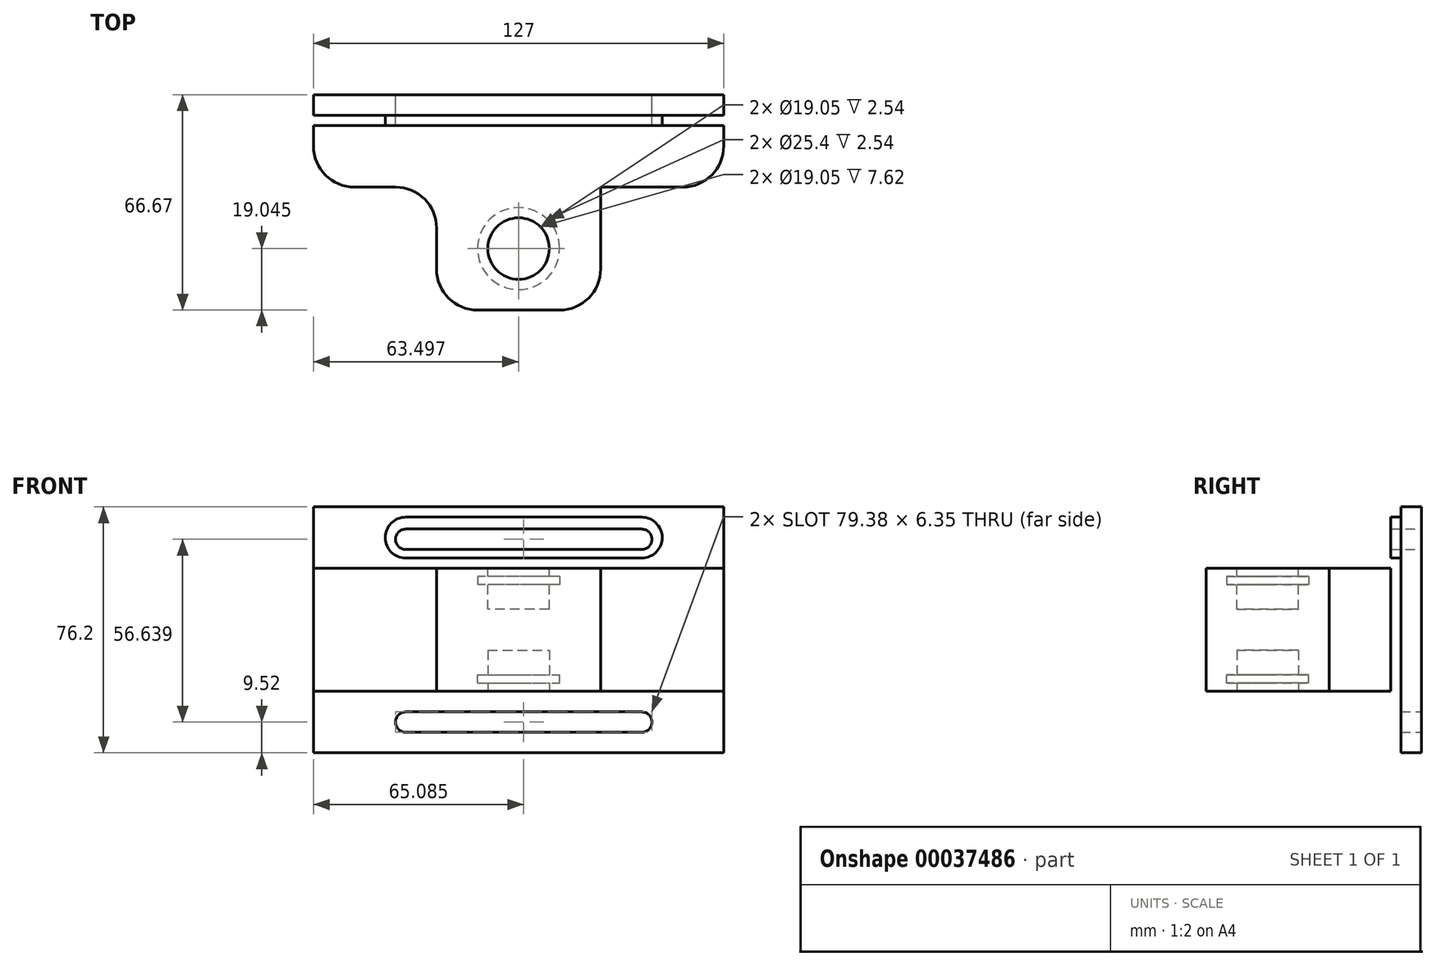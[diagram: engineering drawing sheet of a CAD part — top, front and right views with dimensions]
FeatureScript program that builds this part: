
annotation { "Feature Type Name" : "Feature", "Feature Type Description" : "" }
export const myFeature = defineFeature(function(context is Context, id is Id, definition is map)
    precondition{}
    {
        {
            var Q0;
            Q0=qCreatedBy(makeId("Front.planeOp"),FACE);
            var sketch = newSketch(context, id + "F0", { "sketchPlane" : qUnion([Q0])});
            skLineSegment(sketch, "E0.bottom", {"start": v(-62.5, -34.76) * mm, "end": v(64.5, -34.76) * mm});
            skLineSegment(sketch, "E0.top", {"start": v(-62.5, 41.44) * mm, "end": v(64.5, 41.44) * mm});
            skLineSegment(sketch, "E0.left", {"start": v(-62.5, -34.76) * mm, "end": v(-62.5, 41.44) * mm});
            skLineSegment(sketch, "E0.right", {"start": v(64.5, -34.76) * mm, "end": v(64.5, 41.44) * mm});
            skArc(sketch, "E1", {"start": v(-33.93, -22.06) * mm, "mid": v(-37.1, -25.24) * mm, "end": v(-33.93, -28.41) * mm});
            skArc(sketch, "E2", {"start": v(39.1, -28.41) * mm, "mid": v(42.27, -25.24) * mm, "end": v(39.1, -22.06) * mm});
            skLineSegment(sketch, "E3", {"start": v(-33.93, -22.06) * mm, "end": v(39.1, -22.06) * mm});
            skLineSegment(sketch, "E4", {"start": v(-33.93, -28.41) * mm, "end": v(39.1, -28.41) * mm});
            skLineSegment(sketch, "E5", {"start": v(-62.5, 3.08) * mm, "end": v(64.5, 3.08) * mm, "construction": true});
            skArc(sketch, "E6.MirrorCS", {"start": v(-33.93, 28.22) * mm, "mid": v(-37.1, 31.4) * mm, "end": v(-33.93, 34.57) * mm});
            skLineSegment(sketch, "E7.MirrorCS", {"start": v(-33.93, 28.22) * mm, "end": v(39.1, 28.22) * mm});
            skLineSegment(sketch, "E8.MirrorCS", {"start": v(-33.93, 34.57) * mm, "end": v(39.1, 34.57) * mm});
            skArc(sketch, "E9.MirrorCS", {"start": v(39.1, 34.57) * mm, "mid": v(42.27, 31.4) * mm, "end": v(39.1, 28.22) * mm});
            skSolve(sketch);
        }
        {
            var Q0;
            Q0=makeQuery(id+"F0.imprint","IMPRINT",FACE,{"disambiguationData":[TD([[makeQuery(id+"F0.imprint","IMPRINT",EDGE,{"derivedFrom":sQuery(id+"F0.wireOp",EDGE,"E0.bottom")}),1.0]])]});
            extrude(context, id + "F1", {"entities" : qUnion([Q0]), "depth" : 9.52 * mm});
        }
        {
            var Q0;
            Q0=makeQuery(id+"F1.opExtrude","CAP_FACE",FACE,{"disambiguationData":[OSD([sQuery(id+"F0.wireOp",EDGE,"E0.bottom"),sQuery(id+"F0.wireOp",EDGE,"E0.top"),sQuery(id+"F0.wireOp",EDGE,"E0.left"),sQuery(id+"F0.wireOp",EDGE,"E0.right"),sQuery(id+"F0.wireOp",EDGE,"E1"),sQuery(id+"F0.wireOp",EDGE,"E2"),sQuery(id+"F0.wireOp",EDGE,"E3"),sQuery(id+"F0.wireOp",EDGE,"E4"),sQuery(id+"F0.wireOp",EDGE,"E6.MirrorCS"),sQuery(id+"F0.wireOp",EDGE,"E7.MirrorCS"),sQuery(id+"F0.wireOp",EDGE,"E8.MirrorCS"),sQuery(id+"F0.wireOp",EDGE,"E9.MirrorCS")])],"isStart":false});
            var sketch = newSketch(context, id + "F2", { "sketchPlane" : qUnion([Q0])});
            skArc(sketch, "E10", {"start": v(-33.93, -18.89) * mm, "mid": v(-40.28, -25.24) * mm, "end": v(-33.93, -31.59) * mm});
            skArc(sketch, "E11", {"start": v(39.1, -31.59) * mm, "mid": v(45.45, -25.24) * mm, "end": v(39.1, -18.89) * mm});
            skLineSegment(sketch, "E12", {"start": v(-33.93, -18.89) * mm, "end": v(39.1, -18.89) * mm});
            skLineSegment(sketch, "E13", {"start": v(-33.93, -31.59) * mm, "end": v(39.1, -31.59) * mm});
            skLineSegment(sketch, "E14", {"start": v(-62.5, 3.34) * mm, "end": v(64.5, 3.34) * mm, "construction": true});
            skArc(sketch, "E15.MirrorCS", {"start": v(-33.93, 25.56) * mm, "mid": v(-40.28, 31.91) * mm, "end": v(-33.93, 38.26) * mm});
            skLineSegment(sketch, "E16.MirrorCS", {"start": v(-33.93, 25.56) * mm, "end": v(39.1, 25.56) * mm});
            skLineSegment(sketch, "E17.MirrorCS", {"start": v(-33.93, 38.26) * mm, "end": v(39.1, 38.26) * mm});
            skArc(sketch, "E18.MirrorCS", {"start": v(39.1, 38.26) * mm, "mid": v(45.45, 31.91) * mm, "end": v(39.1, 25.56) * mm});
            skSolve(sketch);
        }
        {
            var Q0;
            Q0=makeQuery(id+"F2.imprint","IMPRINT",FACE,{"disambiguationData":[TD([[makeQuery(id+"F2.imprint","IMPRINT",EDGE,{"derivedFrom":sQuery(id+"F2.wireOp",EDGE,"E10")}),1.0]])]});
            var Q1;
            Q1=makeQuery(id+"F2.imprint","IMPRINT",FACE,{"disambiguationData":[TD([[makeQuery(id+"F2.imprint","IMPRINT",EDGE,{"derivedFrom":sQuery(id+"F2.wireOp",EDGE,"E15.MirrorCS")}),-1.0]])]});
            extrude(context, id + "F3", {"entities" : qUnion([Q0, Q1]), "operationType" : NewBodyOperationType.REMOVE, "oppositeDirection" : true, "depth" : 3.17 * mm});
        }
        {
            var Q0;
            Q0=makeQuery(id+"F1.opExtrude","CAP_FACE",FACE,{"disambiguationData":[OSD([sQuery(id+"F0.wireOp",EDGE,"E0.bottom"),sQuery(id+"F0.wireOp",EDGE,"E0.top"),sQuery(id+"F0.wireOp",EDGE,"E0.left"),sQuery(id+"F0.wireOp",EDGE,"E0.right"),sQuery(id+"F0.wireOp",EDGE,"E1"),sQuery(id+"F0.wireOp",EDGE,"E2"),sQuery(id+"F0.wireOp",EDGE,"E3"),sQuery(id+"F0.wireOp",EDGE,"E4"),sQuery(id+"F0.wireOp",EDGE,"E6.MirrorCS"),sQuery(id+"F0.wireOp",EDGE,"E7.MirrorCS"),sQuery(id+"F0.wireOp",EDGE,"E8.MirrorCS"),sQuery(id+"F0.wireOp",EDGE,"E9.MirrorCS")])],"isStart":false});
            var sketch = newSketch(context, id + "F4", { "sketchPlane" : qUnion([Q0])});
            skLineSegment(sketch, "E19.bottom", {"start": v(-62.5, -15.71) * mm, "end": v(64.5, -15.71) * mm});
            skLineSegment(sketch, "E19.top", {"start": v(-62.5, 22.39) * mm, "end": v(64.5, 22.39) * mm});
            skLineSegment(sketch, "E19.left", {"start": v(-62.5, -15.71) * mm, "end": v(-62.5, 22.39) * mm});
            skLineSegment(sketch, "E19.right", {"start": v(64.5, -15.71) * mm, "end": v(64.5, 22.39) * mm});
            skSolve(sketch);
        }
        {
            var Q0;
            Q0=makeQuery(id+"F4.imprint","IMPRINT",FACE,{"disambiguationData":[TD([[makeQuery(id+"F4.imprint","IMPRINT",EDGE,{"derivedFrom":sQuery(id+"F4.wireOp",EDGE,"E19.bottom")}),1.0]])]});
            extrude(context, id + "F5", {"entities" : qUnion([Q0]), "operationType" : NewBodyOperationType.ADD, "depth" : 19.05 * mm});
        }
        {
            var Q0;
            Q0=makeQuery(id+"F5.opExtrude","CAP_FACE",FACE,{"disambiguationData":[OSD([sQuery(id+"F4.wireOp",EDGE,"E19.bottom"),sQuery(id+"F4.wireOp",EDGE,"E19.top"),sQuery(id+"F4.wireOp",EDGE,"E19.left"),sQuery(id+"F4.wireOp",EDGE,"E19.right")])],"isStart":false});
            var sketch = newSketch(context, id + "F6", { "sketchPlane" : qUnion([Q0])});
            skLineSegment(sketch, "E20.bottom", {"start": v(-24.4, -15.71) * mm, "end": v(26.4, -15.71) * mm});
            skLineSegment(sketch, "E20.top", {"start": v(-24.4, 22.39) * mm, "end": v(26.4, 22.39) * mm});
            skLineSegment(sketch, "E20.left", {"start": v(-24.4, -15.71) * mm, "end": v(-24.4, 22.39) * mm});
            skLineSegment(sketch, "E20.right", {"start": v(26.4, -15.71) * mm, "end": v(26.4, 22.39) * mm});
            skSolve(sketch);
        }
        {
            var Q0;
            Q0=makeQuery(id+"F6.imprint","IMPRINT",FACE,{"disambiguationData":[TD([[makeQuery(id+"F6.imprint","IMPRINT",EDGE,{"derivedFrom":sQuery(id+"F6.wireOp",EDGE,"E20.bottom")}),1.0]])]});
            extrude(context, id + "F7", {"entities" : qUnion([Q0]), "operationType" : NewBodyOperationType.ADD, "depth" : 38.1 * mm});
        }
        {
            var Q0;
            Q0=makeQuery(id+"F7.boolean.opBoolean","MERGE",FACE,{"derivedFrom":[makeQuery(id+"F5.opExtrude","SWEPT_FACE",FACE,{"disambiguationData":[OSD([sQuery(id+"F4.wireOp",EDGE,"E19.bottom")])]}),makeQuery(id+"F7.opExtrude","SWEPT_FACE",FACE,{"disambiguationData":[OSD([sQuery(id+"F6.wireOp",EDGE,"E20.bottom")])]})]});
            var sketch = newSketch(context, id + "F8", { "sketchPlane" : qUnion([Q0])});
            skPoint(sketch, "E21", {"position": v(1, 47.63) * mm});
            skSolve(sketch);
        }
        {
            var Q0;
            Q0=sQuery(id+"F8.wireOp",VERTEX,"E21");
            var Q1;
            Q1=makeQuery(id+"F1.opExtrude","SWEPT_BODY",BODY,{"disambiguationData":[OSD([sQuery(id+"F0.wireOp",EDGE,"E0.bottom"),sQuery(id+"F0.wireOp",EDGE,"E0.top"),sQuery(id+"F0.wireOp",EDGE,"E0.left"),sQuery(id+"F0.wireOp",EDGE,"E0.right"),sQuery(id+"F0.wireOp",EDGE,"E1"),sQuery(id+"F0.wireOp",EDGE,"E2"),sQuery(id+"F0.wireOp",EDGE,"E3"),sQuery(id+"F0.wireOp",EDGE,"E4"),sQuery(id+"F0.wireOp",EDGE,"E6.MirrorCS"),sQuery(id+"F0.wireOp",EDGE,"E7.MirrorCS"),sQuery(id+"F0.wireOp",EDGE,"E8.MirrorCS"),sQuery(id+"F0.wireOp",EDGE,"E9.MirrorCS")])]});
            hole(context, id + "F9", {"style" : HoleStyle.SIMPLE, "holeDiameter" : 9.52 * mm, "endStyle" : HoleEndStyle.THROUGH, "locations" : qUnion([Q0]), "scope" : qUnion([Q1])});
        }
        {
            var Q0;
            Q0=makeQuery(id+"F7.boolean.opBoolean","MERGE",FACE,{"derivedFrom":[makeQuery(id+"F5.opExtrude","SWEPT_FACE",FACE,{"disambiguationData":[OSD([sQuery(id+"F4.wireOp",EDGE,"E19.bottom")])]}),makeQuery(id+"F7.opExtrude","SWEPT_FACE",FACE,{"disambiguationData":[OSD([sQuery(id+"F6.wireOp",EDGE,"E20.bottom")])]})]});
            var sketch = newSketch(context, id + "F10", { "sketchPlane" : qUnion([Q0])});
            skCircle(sketch, "E22", {"center": v(1, 47.63) * mm, "radius": 9.53 * mm});
            skSolve(sketch);
        }
        {
            var Q0;
            Q0=makeQuery(id+"F10.imprint","IMPRINT",FACE,{"disambiguationData":[TD([[makeQuery(id+"F10.imprint","IMPRINT",EDGE,{"derivedFrom":sQuery(id+"F10.wireOp",EDGE,"E22")}),1.0]])]});
            extrude(context, id + "F11", {"entities" : qUnion([Q0]), "operationType" : NewBodyOperationType.REMOVE, "oppositeDirection" : true, "depth" : 12.7 * mm});
        }
        {
            var Q0;
            Q0=makeQuery(id+"F7.boolean.opBoolean","MERGE",FACE,{"derivedFrom":[makeQuery(id+"F5.opExtrude","SWEPT_FACE",FACE,{"disambiguationData":[OSD([sQuery(id+"F4.wireOp",EDGE,"E19.top")])]}),makeQuery(id+"F7.opExtrude","SWEPT_FACE",FACE,{"disambiguationData":[OSD([sQuery(id+"F6.wireOp",EDGE,"E20.top")])]})]});
            var sketch = newSketch(context, id + "F12", { "sketchPlane" : qUnion([Q0])});
            skCircle(sketch, "E23", {"center": v(1, -47.63) * mm, "radius": 9.53 * mm});
            skSolve(sketch);
        }
        {
            var Q0;
            Q0 = qSketchRegion(id + "F12", true);
            var Q1;
            Q1=makeQuery(id+"F12.imprint","IMPRINT",FACE,{"disambiguationData":[TD([[makeQuery(id+"F12.imprint","IMPRINT",EDGE,{"derivedFrom":sQuery(id+"F12.wireOp",EDGE,"E23")}),1.0]])]});
            extrude(context, id + "F13", {"entities" : qUnion([Q0, Q1]), "operationType" : NewBodyOperationType.REMOVE, "oppositeDirection" : true, "depth" : 12.7 * mm});
        }
        {
            var Q0;
            Q0=makeQuery(id+"F1.opExtrude","SWEPT_FACE",FACE,{"disambiguationData":[OSD([sQuery(id+"F0.wireOp",EDGE,"E0.top")])]});
            cPlane(context, id + "F14", {"entities" : qUnion([Q0]), "cplaneType" : CPlaneType.OFFSET, "offset" : 24.13 * mm, "oppositeDirection" : true, "width" : 152.4 * mm, "height" : 152.4 * mm});
        }
        {
            var Q0;
            Q0=qCreatedBy(id+"F14.planeOp",FACE);
            var sketch = newSketch(context, id + "F15", { "sketchPlane" : qUnion([Q0])});
            skCircle(sketch, "E24", {"center": v(1, -47.63) * mm, "radius": 12.7 * mm});
            skSolve(sketch);
        }
        {
            var Q0;
            Q0=makeQuery(id+"F1.opExtrude","SWEPT_FACE",FACE,{"disambiguationData":[OSD([sQuery(id+"F0.wireOp",EDGE,"E0.bottom")])]});
            cPlane(context, id + "F16", {"entities" : qUnion([Q0]), "cplaneType" : CPlaneType.OFFSET, "offset" : 24.13 * mm, "oppositeDirection" : true, "width" : 152.4 * mm, "height" : 152.4 * mm});
        }
        {
            var Q0;
            Q0=qCreatedBy(id+"F16.planeOp",FACE);
            var sketch = newSketch(context, id + "F17", { "sketchPlane" : qUnion([Q0])});
            skCircle(sketch, "E25.0", {"center": v(1, 47.63) * mm, "radius": 12.7 * mm});
            skSolve(sketch);
        }
        {
            var Q0;
            Q0 = qSketchRegion(id + "F17", true);
            var Q1;
            Q1=makeQuery(id+"F7.boolean.opBoolean","MERGE",FACE,{"derivedFrom":[makeQuery(id+"F5.opExtrude","SWEPT_FACE",FACE,{"disambiguationData":[OSD([sQuery(id+"F4.wireOp",EDGE,"E19.bottom")])]}),makeQuery(id+"F7.opExtrude","SWEPT_FACE",FACE,{"disambiguationData":[OSD([sQuery(id+"F6.wireOp",EDGE,"E20.bottom")])]})]});
            extrude(context, id + "F18", {"entities" : qUnion([Q0, Q1]), "operationType" : NewBodyOperationType.REMOVE, "depth" : 2.54 * mm});
        }
        {
            var Q0;
            Q0 = qSketchRegion(id + "F15", true);
            var Q1;
            Q1=makeQuery(id+"F7.boolean.opBoolean","MERGE",FACE,{"derivedFrom":[makeQuery(id+"F5.opExtrude","SWEPT_FACE",FACE,{"disambiguationData":[OSD([sQuery(id+"F4.wireOp",EDGE,"E19.top")])]}),makeQuery(id+"F7.opExtrude","SWEPT_FACE",FACE,{"disambiguationData":[OSD([sQuery(id+"F6.wireOp",EDGE,"E20.top")])]})]});
            extrude(context, id + "F19", {"entities" : qUnion([Q0, Q1]), "operationType" : NewBodyOperationType.REMOVE, "depth" : 2.54 * mm});
        }
        {
            var Q0;
            Q0=makeQuery(id+"F5.opExtrude","CAP_EDGE",EDGE,{"disambiguationData":[OSD([sQuery(id+"F4.wireOp",EDGE,"E19.left")])],"isStart":false});
            var Q1;
            Q1=makeQuery(id+"F7.opExtrude","CAP_EDGE",EDGE,{"disambiguationData":[OSD([sQuery(id+"F6.wireOp",EDGE,"E20.left")])],"isStart":true});
            var Q2;
            Q2=makeQuery(id+"F7.opExtrude","CAP_EDGE",EDGE,{"disambiguationData":[OSD([sQuery(id+"F6.wireOp",EDGE,"E20.left")])],"isStart":false});
            var Q3;
            Q3=makeQuery(id+"F7.opExtrude","CAP_EDGE",EDGE,{"disambiguationData":[OSD([sQuery(id+"F6.wireOp",EDGE,"E20.right")])],"isStart":false});
            var Q4;
            Q4=makeQuery(id+"F7.opExtrude","CAP_EDGE",EDGE,{"disambiguationData":[OSD([sQuery(id+"F6.wireOp",EDGE,"E20.right")])],"isStart":true});
            fillet(context, id + "F20", {"entities" : qUnion([Q0, Q1, Q2, Q3, Q4]), "radius" : 12.7 * mm, "tangentPropagation" : true, "allowEdgeOverflow" : false});
        }
        {
            var Q0;
            Q0=makeQuery(id+"F5.opExtrude","CAP_EDGE",EDGE,{"disambiguationData":[OSD([sQuery(id+"F4.wireOp",EDGE,"E19.right")])],"isStart":false});
            fillet(context, id + "F21", {"entities" : qUnion([Q0]), "radius" : 12.7 * mm, "tangentPropagation" : true, "allowEdgeOverflow" : false});
        }
    });
